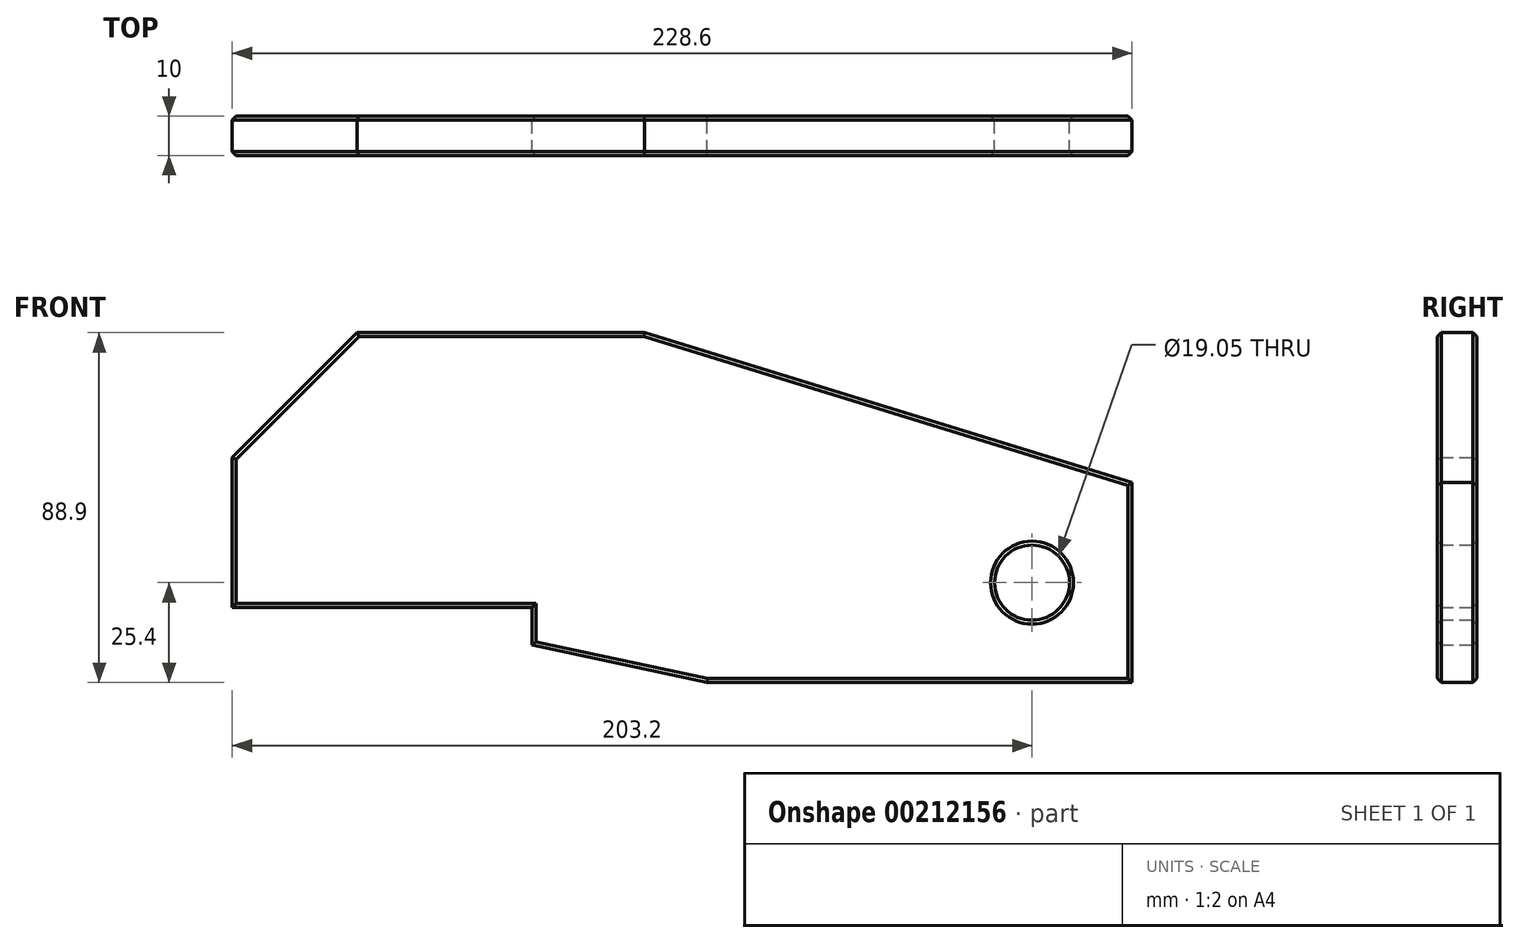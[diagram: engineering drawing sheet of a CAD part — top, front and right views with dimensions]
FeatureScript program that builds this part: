
annotation { "Feature Type Name" : "Feature", "Feature Type Description" : "" }
export const myFeature = defineFeature(function(context is Context, id is Id, definition is map)
    precondition{}
    {
        {
            var Q0;
            Q0=qCreatedBy(makeId("Front.planeOp"),FACE);
            var sketch = newSketch(context, id + "F0", { "sketchPlane" : qUnion([Q0])});
            skLineSegment(sketch, "E0", {"start": v(0, 0) * mm, "end": v(0, 38.1) * mm});
            skLineSegment(sketch, "E1", {"start": v(0, 38.1) * mm, "end": v(31.75, 69.85) * mm});
            skLineSegment(sketch, "E2", {"start": v(31.75, 69.85) * mm, "end": v(104.78, 69.85) * mm});
            skLineSegment(sketch, "E3", {"start": v(104.77, 69.85) * mm, "end": v(228.6, 31.75) * mm});
            skLineSegment(sketch, "E4", {"start": v(228.6, 31.75) * mm, "end": v(228.6, -19.05) * mm});
            skLineSegment(sketch, "E5", {"start": v(228.6, -19.05) * mm, "end": v(120.65, -19.05) * mm});
            skLineSegment(sketch, "E6", {"start": v(0, 0) * mm, "end": v(76.2, 0) * mm});
            skLineSegment(sketch, "E7", {"start": v(76.2, 0) * mm, "end": v(76.2, -9.53) * mm});
            skLineSegment(sketch, "E8", {"start": v(76.2, -9.53) * mm, "end": v(120.65, -19.05) * mm});
            skPoint(sketch, "E9", {"position": v(203.2, 6.35) * mm});
            skCircle(sketch, "E10", {"center": v(203.2, 6.35) * mm, "radius": 9.53 * mm});
            skSolve(sketch);
        }
        {
            var Q0;
            Q0=makeQuery(id+"F0.imprint","IMPRINT",FACE,{"disambiguationData":[TD([[makeQuery(id+"F0.imprint","IMPRINT",EDGE,{"derivedFrom":sQuery(id+"F0.wireOp",EDGE,"SEA8ICYz-lSKE-FzLg-bkjO-wskU425YcoNz")}),-1.0]])]});
            var Q1;
            Q1=makeQuery(id+"F0.imprint","IMPRINT",FACE,{"disambiguationData":[TD([[makeQuery(id+"F0.imprint","IMPRINT",EDGE,{"derivedFrom":sQuery(id+"F0.wireOp",EDGE,"E0")}),-1.0]])]});
            extrude(context, id + "F1", {"entities" : qUnion([Q0, Q1]), "depth" : 10 * mm});
        }
        {
            var Q0;
            Q0=makeQuery(id+"F1.opExtrude","CAP_FACE",FACE,{"disambiguationData":[OSD([sQuery(id+"F0.wireOp",EDGE,"E0"),sQuery(id+"F0.wireOp",EDGE,"E1"),sQuery(id+"F0.wireOp",EDGE,"E2"),sQuery(id+"F0.wireOp",EDGE,"E3"),sQuery(id+"F0.wireOp",EDGE,"E4"),sQuery(id+"F0.wireOp",EDGE,"E5"),sQuery(id+"F0.wireOp",EDGE,"E6"),sQuery(id+"F0.wireOp",EDGE,"E7"),sQuery(id+"F0.wireOp",EDGE,"E8"),sQuery(id+"F0.wireOp",EDGE,"E10")])],"isStart":false});
            var Q1;
            Q1=makeQuery(id+"F1.opExtrude","CAP_FACE",FACE,{"disambiguationData":[OSD([sQuery(id+"F0.wireOp",EDGE,"E0"),sQuery(id+"F0.wireOp",EDGE,"E1"),sQuery(id+"F0.wireOp",EDGE,"E2"),sQuery(id+"F0.wireOp",EDGE,"E3"),sQuery(id+"F0.wireOp",EDGE,"E4"),sQuery(id+"F0.wireOp",EDGE,"E5"),sQuery(id+"F0.wireOp",EDGE,"E6"),sQuery(id+"F0.wireOp",EDGE,"E7"),sQuery(id+"F0.wireOp",EDGE,"E8"),sQuery(id+"F0.wireOp",EDGE,"E10")])],"isStart":true});
            chamfer(context, id + "F2", {"entities" : qUnion([Q0, Q1]), "width" : 1.02 * mm, "tangentPropagation" : true});
        }
    });
